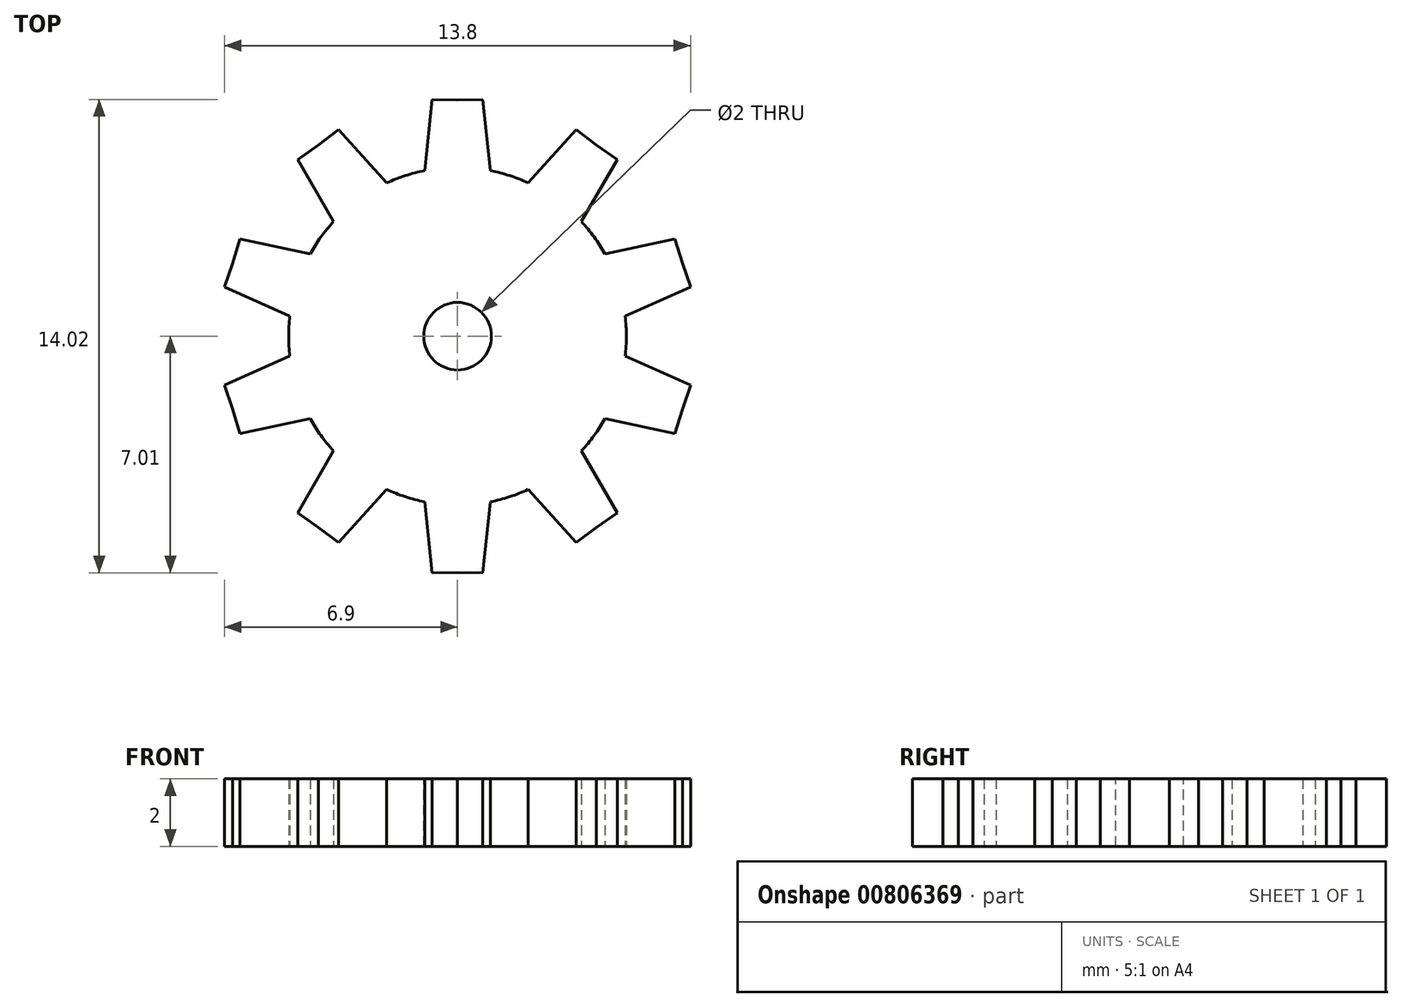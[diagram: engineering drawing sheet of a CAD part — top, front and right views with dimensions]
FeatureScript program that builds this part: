
annotation { "Feature Type Name" : "Feature", "Feature Type Description" : "" }
export const myFeature = defineFeature(function(context is Context, id is Id, definition is map)
    precondition{}
    {
        {
            var Q0;
            Q0=qCreatedBy(makeId("Top.planeOp"),FACE);
            var sketch = newSketch(context, id + "F0", { "sketchPlane" : qUnion([Q0])});
            skCircle(sketch, "E0", {"center": v(0, 0) * mm, "radius": 5 * mm});
            skLineSegment(sketch, "E1", {"start": v(0, 0) * mm, "end": v(0, 5) * mm, "construction": true});
            skPoint(sketch, "E2.end.orphan", {"position": v(0, 7) * mm});
            skPoint(sketch, "E3.end.orphan", {"position": v(-1.37, 9.64) * mm});
            skPoint(sketch, "E3.start.orphan", {"position": v(-0.97, 4.9) * mm});
            skPoint(sketch, "E4.MirrorCS.start.orphan", {"position": v(1.37, 9.64) * mm});
            skPoint(sketch, "E5.MirrorCS.start.orphan", {"position": v(0.97, 4.9) * mm});
            skLineSegment(sketch, "E6", {"start": v(-0.97, 4.9) * mm, "end": v(-0.75, 7.01) * mm});
            skLineSegment(sketch, "E7", {"start": v(-0.75, 7.01) * mm, "end": v(0, 7) * mm});
            skLineSegment(sketch, "E8.MirrorCS", {"start": v(0.97, 4.9) * mm, "end": v(0.75, 7.01) * mm});
            skLineSegment(sketch, "E9.MirrorCS", {"start": v(0.75, 7.01) * mm, "end": v(0, 7) * mm});
            skLineSegment(sketch, "E10.1.0", {"start": v(-3.67, 3.4) * mm, "end": v(-4.73, 5.23) * mm});
            skLineSegment(sketch, "E10.1.1", {"start": v(-4.73, 5.23) * mm, "end": v(-4.11, 5.66) * mm});
            skLineSegment(sketch, "E10.1.2", {"start": v(-3.52, 6.12) * mm, "end": v(-4.11, 5.66) * mm});
            skLineSegment(sketch, "E10.1.3", {"start": v(-2.1, 4.54) * mm, "end": v(-3.52, 6.12) * mm});
            skLineSegment(sketch, "E10.2.0", {"start": v(-4.97, 0.6) * mm, "end": v(-6.9, 1.45) * mm});
            skLineSegment(sketch, "E10.2.1", {"start": v(-6.9, 1.45) * mm, "end": v(-6.66, 2.16) * mm});
            skLineSegment(sketch, "E10.2.2", {"start": v(-6.44, 2.88) * mm, "end": v(-6.66, 2.16) * mm});
            skLineSegment(sketch, "E10.2.3", {"start": v(-4.36, 2.44) * mm, "end": v(-6.44, 2.88) * mm});
            skLineSegment(sketch, "E10.3.0", {"start": v(-4.36, -2.44) * mm, "end": v(-6.44, -2.88) * mm});
            skLineSegment(sketch, "E10.3.1", {"start": v(-6.44, -2.88) * mm, "end": v(-6.66, -2.16) * mm});
            skLineSegment(sketch, "E10.3.2", {"start": v(-6.9, -1.45) * mm, "end": v(-6.66, -2.16) * mm});
            skLineSegment(sketch, "E10.3.3", {"start": v(-4.97, -0.6) * mm, "end": v(-6.9, -1.45) * mm});
            skLineSegment(sketch, "E10.4.0", {"start": v(-2.1, -4.54) * mm, "end": v(-3.52, -6.12) * mm});
            skLineSegment(sketch, "E10.4.1", {"start": v(-3.52, -6.12) * mm, "end": v(-4.11, -5.66) * mm});
            skLineSegment(sketch, "E10.4.2", {"start": v(-4.73, -5.23) * mm, "end": v(-4.11, -5.66) * mm});
            skLineSegment(sketch, "E10.4.3", {"start": v(-3.67, -3.4) * mm, "end": v(-4.73, -5.23) * mm});
            skLineSegment(sketch, "E10.5.0", {"start": v(0.97, -4.9) * mm, "end": v(0.75, -7.01) * mm});
            skLineSegment(sketch, "E10.5.1", {"start": v(0.75, -7.01) * mm, "end": v(0, -7) * mm});
            skLineSegment(sketch, "E10.5.2", {"start": v(-0.75, -7.01) * mm, "end": v(0, -7) * mm});
            skLineSegment(sketch, "E10.5.3", {"start": v(-0.97, -4.9) * mm, "end": v(-0.75, -7.01) * mm});
            skLineSegment(sketch, "E10.6.0", {"start": v(3.67, -3.4) * mm, "end": v(4.73, -5.23) * mm});
            skLineSegment(sketch, "E10.6.1", {"start": v(4.73, -5.23) * mm, "end": v(4.11, -5.66) * mm});
            skLineSegment(sketch, "E10.6.2", {"start": v(3.52, -6.12) * mm, "end": v(4.11, -5.66) * mm});
            skLineSegment(sketch, "E10.6.3", {"start": v(2.1, -4.54) * mm, "end": v(3.52, -6.12) * mm});
            skLineSegment(sketch, "E10.7.0", {"start": v(4.97, -0.6) * mm, "end": v(6.9, -1.45) * mm});
            skLineSegment(sketch, "E10.7.1", {"start": v(6.9, -1.45) * mm, "end": v(6.66, -2.16) * mm});
            skLineSegment(sketch, "E10.7.2", {"start": v(6.44, -2.88) * mm, "end": v(6.66, -2.16) * mm});
            skLineSegment(sketch, "E10.7.3", {"start": v(4.36, -2.44) * mm, "end": v(6.44, -2.88) * mm});
            skLineSegment(sketch, "E10.8.0", {"start": v(4.36, 2.44) * mm, "end": v(6.44, 2.88) * mm});
            skLineSegment(sketch, "E10.8.1", {"start": v(6.44, 2.88) * mm, "end": v(6.66, 2.16) * mm});
            skLineSegment(sketch, "E10.8.2", {"start": v(6.9, 1.45) * mm, "end": v(6.66, 2.16) * mm});
            skLineSegment(sketch, "E10.8.3", {"start": v(4.97, 0.6) * mm, "end": v(6.9, 1.45) * mm});
            skLineSegment(sketch, "E10.9.0", {"start": v(2.1, 4.54) * mm, "end": v(3.52, 6.12) * mm});
            skLineSegment(sketch, "E10.9.1", {"start": v(3.52, 6.12) * mm, "end": v(4.11, 5.66) * mm});
            skLineSegment(sketch, "E10.9.2", {"start": v(4.73, 5.23) * mm, "end": v(4.11, 5.66) * mm});
            skLineSegment(sketch, "E10.9.3", {"start": v(3.67, 3.4) * mm, "end": v(4.73, 5.23) * mm});
            skSolve(sketch);
        }
        {
            var Q0;
            Q0=qSketchRegion(id+"F0",true);
            extrude(context, id + "F1", {"entities" : qUnion([Q0]), "depth" : 2 * mm, "offsetDistance" : 25 * mm});
        }
        {
            var Q0;
            Q0=makeQuery(id+"F1.opExtrude","CAP_FACE",FACE,{"disambiguationData":[OSD([sQuery(id+"F0.wireOp",EDGE,"E0"),sQuery(id+"F0.wireOp",EDGE,"E6"),sQuery(id+"F0.wireOp",EDGE,"E7"),sQuery(id+"F0.wireOp",EDGE,"E8.MirrorCS"),sQuery(id+"F0.wireOp",EDGE,"E9.MirrorCS"),sQuery(id+"F0.wireOp",EDGE,"E10.1.0"),sQuery(id+"F0.wireOp",EDGE,"E10.1.1"),sQuery(id+"F0.wireOp",EDGE,"E10.1.2"),sQuery(id+"F0.wireOp",EDGE,"E10.1.3"),sQuery(id+"F0.wireOp",EDGE,"E10.2.0"),sQuery(id+"F0.wireOp",EDGE,"E10.2.1"),sQuery(id+"F0.wireOp",EDGE,"E10.2.2"),sQuery(id+"F0.wireOp",EDGE,"E10.2.3"),sQuery(id+"F0.wireOp",EDGE,"E10.3.0"),sQuery(id+"F0.wireOp",EDGE,"E10.3.1"),sQuery(id+"F0.wireOp",EDGE,"E10.3.2"),sQuery(id+"F0.wireOp",EDGE,"E10.3.3"),sQuery(id+"F0.wireOp",EDGE,"E10.4.0"),sQuery(id+"F0.wireOp",EDGE,"E10.4.1"),sQuery(id+"F0.wireOp",EDGE,"E10.4.2"),sQuery(id+"F0.wireOp",EDGE,"E10.4.3"),sQuery(id+"F0.wireOp",EDGE,"E10.5.0"),sQuery(id+"F0.wireOp",EDGE,"E10.5.1"),sQuery(id+"F0.wireOp",EDGE,"E10.5.2"),sQuery(id+"F0.wireOp",EDGE,"E10.5.3"),sQuery(id+"F0.wireOp",EDGE,"E10.6.0"),sQuery(id+"F0.wireOp",EDGE,"E10.6.1"),sQuery(id+"F0.wireOp",EDGE,"E10.6.2"),sQuery(id+"F0.wireOp",EDGE,"E10.6.3"),sQuery(id+"F0.wireOp",EDGE,"E10.7.0"),sQuery(id+"F0.wireOp",EDGE,"E10.7.1"),sQuery(id+"F0.wireOp",EDGE,"E10.7.2"),sQuery(id+"F0.wireOp",EDGE,"E10.7.3"),sQuery(id+"F0.wireOp",EDGE,"E10.8.0"),sQuery(id+"F0.wireOp",EDGE,"E10.8.1"),sQuery(id+"F0.wireOp",EDGE,"E10.8.2"),sQuery(id+"F0.wireOp",EDGE,"E10.8.3"),sQuery(id+"F0.wireOp",EDGE,"E10.9.0"),sQuery(id+"F0.wireOp",EDGE,"E10.9.1"),sQuery(id+"F0.wireOp",EDGE,"E10.9.2"),sQuery(id+"F0.wireOp",EDGE,"E10.9.3"),sQuery(id+"F0.wireOp",EDGE,"E10.10.0"),sQuery(id+"F0.wireOp",EDGE,"E10.10.1"),sQuery(id+"F0.wireOp",EDGE,"E10.10.2"),sQuery(id+"F0.wireOp",EDGE,"E10.10.3"),sQuery(id+"F0.wireOp",EDGE,"E10.11.0"),sQuery(id+"F0.wireOp",EDGE,"E10.11.1"),sQuery(id+"F0.wireOp",EDGE,"E10.11.2"),sQuery(id+"F0.wireOp",EDGE,"E10.11.3"),sQuery(id+"F0.wireOp",EDGE,"E10.12.0"),sQuery(id+"F0.wireOp",EDGE,"E10.12.1"),sQuery(id+"F0.wireOp",EDGE,"E10.12.2"),sQuery(id+"F0.wireOp",EDGE,"E10.12.3"),sQuery(id+"F0.wireOp",EDGE,"E10.13.0"),sQuery(id+"F0.wireOp",EDGE,"E10.13.1"),sQuery(id+"F0.wireOp",EDGE,"E10.13.2"),sQuery(id+"F0.wireOp",EDGE,"E10.13.3"),sQuery(id+"F0.wireOp",EDGE,"E10.14.0"),sQuery(id+"F0.wireOp",EDGE,"E10.14.1"),sQuery(id+"F0.wireOp",EDGE,"E10.14.2"),sQuery(id+"F0.wireOp",EDGE,"E10.14.3"),sQuery(id+"F0.wireOp",EDGE,"E10.15.0"),sQuery(id+"F0.wireOp",EDGE,"E10.15.1"),sQuery(id+"F0.wireOp",EDGE,"E10.15.2"),sQuery(id+"F0.wireOp",EDGE,"E10.15.3")])],"isStart":false});
            var sketch = newSketch(context, id + "F2", { "sketchPlane" : qUnion([Q0])});
            skCircle(sketch, "E11", {"center": v(0, 0) * mm, "radius": 1 * mm});
            skSolve(sketch);
        }
        {
            var Q0;
            Q0=qSketchRegion(id+"F2",true);
            extrude(context, id + "F3", {"entities" : qUnion([Q0]), "operationType" : NewBodyOperationType.REMOVE, "endBound" : BoundingType.THROUGH_ALL, "oppositeDirection" : true, "depth" : 25 * mm, "offsetDistance" : 25 * mm});
        }
    });
